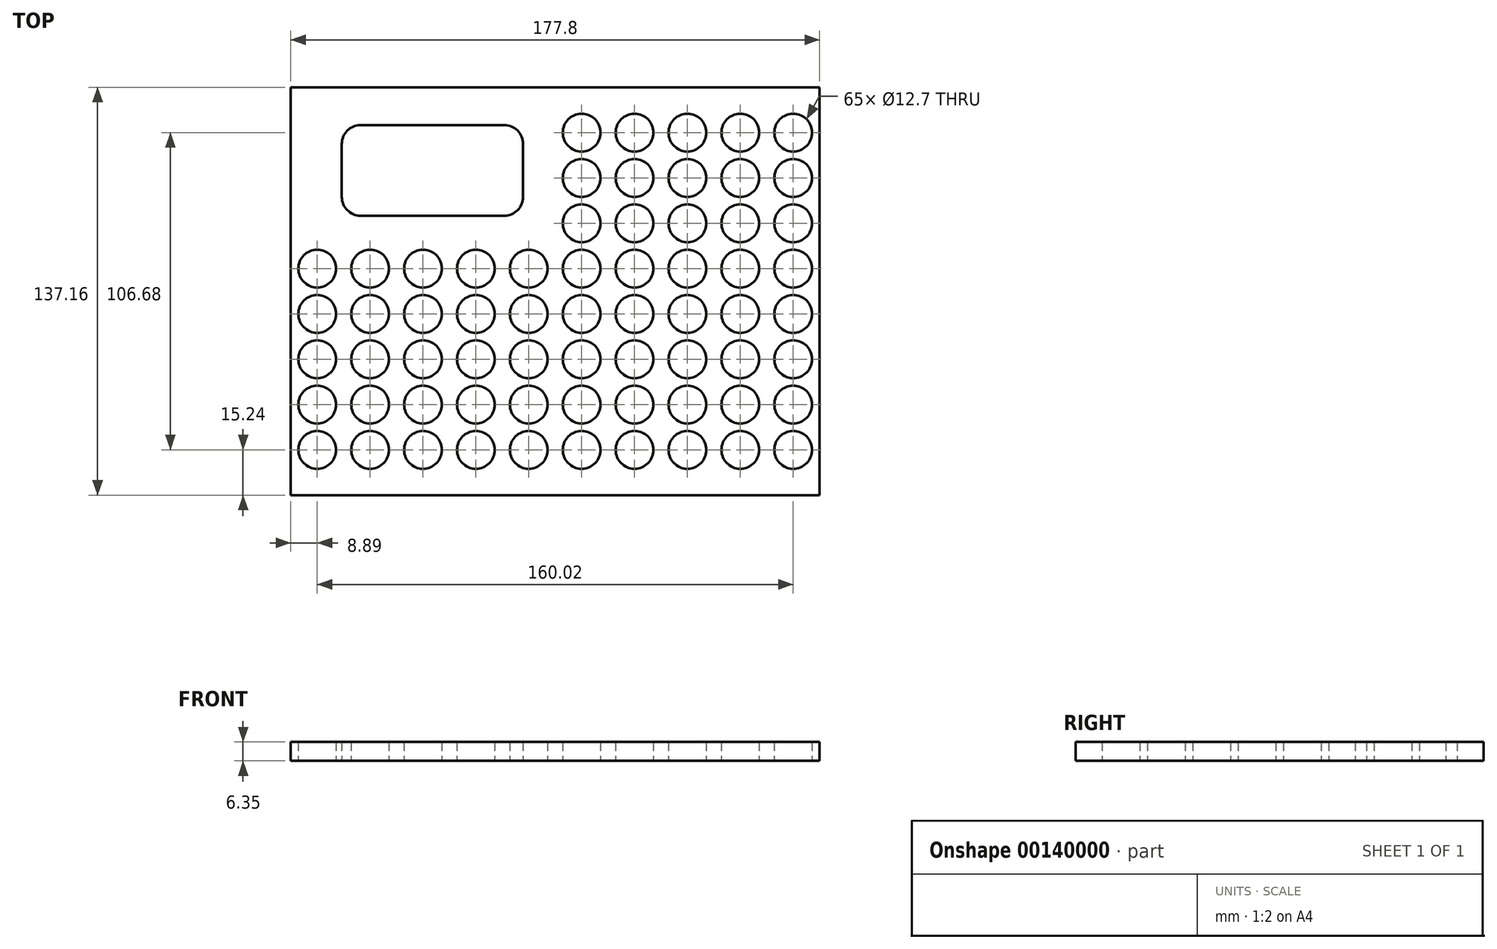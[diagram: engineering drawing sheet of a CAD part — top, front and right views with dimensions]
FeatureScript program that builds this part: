
annotation { "Feature Type Name" : "Feature", "Feature Type Description" : "" }
export const myFeature = defineFeature(function(context is Context, id is Id, definition is map)
    precondition{}
    {
        {
            var Q0;
            Q0=qCreatedBy(makeId("Top.planeOp"),FACE);
            var sketch = newSketch(context, id + "F0", { "sketchPlane" : qUnion([Q0])});
            skCircle(sketch, "E0", {"center": v(0, 0) * mm, "radius": 6.35 * mm});
            skCircle(sketch, "E1.0.1.0", {"center": v(0, 15.24) * mm, "radius": 6.35 * mm});
            skCircle(sketch, "E1.0.2.0", {"center": v(0, 30.48) * mm, "radius": 6.35 * mm});
            skCircle(sketch, "E1.0.3.0", {"center": v(0, 45.72) * mm, "radius": 6.35 * mm});
            skCircle(sketch, "E1.0.4.0", {"center": v(0, 60.96) * mm, "radius": 6.35 * mm});
            skCircle(sketch, "E1.1.0.0", {"center": v(17.78, 0) * mm, "radius": 6.35 * mm});
            skCircle(sketch, "E1.1.1.0", {"center": v(17.78, 15.24) * mm, "radius": 6.35 * mm});
            skCircle(sketch, "E1.1.2.0", {"center": v(17.78, 30.48) * mm, "radius": 6.35 * mm});
            skCircle(sketch, "E1.1.3.0", {"center": v(17.78, 45.72) * mm, "radius": 6.35 * mm});
            skCircle(sketch, "E1.1.4.0", {"center": v(17.78, 60.96) * mm, "radius": 6.35 * mm});
            skCircle(sketch, "E1.2.0.0", {"center": v(35.56, 0) * mm, "radius": 6.35 * mm});
            skCircle(sketch, "E1.2.1.0", {"center": v(35.56, 15.24) * mm, "radius": 6.35 * mm});
            skCircle(sketch, "E1.2.2.0", {"center": v(35.56, 30.48) * mm, "radius": 6.35 * mm});
            skCircle(sketch, "E1.2.3.0", {"center": v(35.56, 45.72) * mm, "radius": 6.35 * mm});
            skCircle(sketch, "E1.2.4.0", {"center": v(35.56, 60.96) * mm, "radius": 6.35 * mm});
            skCircle(sketch, "E1.3.0.0", {"center": v(53.34, 0) * mm, "radius": 6.35 * mm});
            skCircle(sketch, "E1.3.1.0", {"center": v(53.34, 15.24) * mm, "radius": 6.35 * mm});
            skCircle(sketch, "E1.3.2.0", {"center": v(53.34, 30.48) * mm, "radius": 6.35 * mm});
            skCircle(sketch, "E1.3.3.0", {"center": v(53.34, 45.72) * mm, "radius": 6.35 * mm});
            skCircle(sketch, "E1.3.4.0", {"center": v(53.34, 60.96) * mm, "radius": 6.35 * mm});
            skCircle(sketch, "E1.4.0.0", {"center": v(71.12, 0) * mm, "radius": 6.35 * mm});
            skCircle(sketch, "E1.4.1.0", {"center": v(71.12, 15.24) * mm, "radius": 6.35 * mm});
            skCircle(sketch, "E1.4.2.0", {"center": v(71.12, 30.48) * mm, "radius": 6.35 * mm});
            skCircle(sketch, "E1.4.3.0", {"center": v(71.12, 45.72) * mm, "radius": 6.35 * mm});
            skCircle(sketch, "E1.4.4.0", {"center": v(71.12, 60.96) * mm, "radius": 6.35 * mm});
            skCircle(sketch, "E1.5.0.0", {"center": v(88.9, 0) * mm, "radius": 6.35 * mm});
            skCircle(sketch, "E1.5.1.0", {"center": v(88.9, 15.24) * mm, "radius": 6.35 * mm});
            skCircle(sketch, "E1.5.2.0", {"center": v(88.9, 30.48) * mm, "radius": 6.35 * mm});
            skCircle(sketch, "E1.5.3.0", {"center": v(88.9, 45.72) * mm, "radius": 6.35 * mm});
            skCircle(sketch, "E1.5.4.0", {"center": v(88.9, 60.96) * mm, "radius": 6.35 * mm});
            skCircle(sketch, "E1.6.0.0", {"center": v(106.68, 0) * mm, "radius": 6.35 * mm});
            skCircle(sketch, "E1.6.1.0", {"center": v(106.68, 15.24) * mm, "radius": 6.35 * mm});
            skCircle(sketch, "E1.6.2.0", {"center": v(106.68, 30.48) * mm, "radius": 6.35 * mm});
            skCircle(sketch, "E1.6.3.0", {"center": v(106.68, 45.72) * mm, "radius": 6.35 * mm});
            skCircle(sketch, "E1.6.4.0", {"center": v(106.68, 60.96) * mm, "radius": 6.35 * mm});
            skCircle(sketch, "E1.7.0.0", {"center": v(124.46, 0) * mm, "radius": 6.35 * mm});
            skCircle(sketch, "E1.7.1.0", {"center": v(124.46, 15.24) * mm, "radius": 6.35 * mm});
            skCircle(sketch, "E1.7.2.0", {"center": v(124.46, 30.48) * mm, "radius": 6.35 * mm});
            skCircle(sketch, "E1.7.3.0", {"center": v(124.46, 45.72) * mm, "radius": 6.35 * mm});
            skCircle(sketch, "E1.7.4.0", {"center": v(124.46, 60.96) * mm, "radius": 6.35 * mm});
            skLineSegment(sketch, "E1.direction1", {"start": v(0, 0) * mm, "end": v(17.78, 0) * mm, "construction": true});
            skLineSegment(sketch, "E1.direction2", {"start": v(0, 0) * mm, "end": v(0, 15.24) * mm, "construction": true});
            skCircle(sketch, "E2.0.8.0", {"center": v(142.24, 0) * mm, "radius": 6.35 * mm});
            skCircle(sketch, "E2.0.8.1", {"center": v(142.24, 15.24) * mm, "radius": 6.35 * mm});
            skCircle(sketch, "E2.0.8.2", {"center": v(142.24, 30.48) * mm, "radius": 6.35 * mm});
            skCircle(sketch, "E2.0.8.3", {"center": v(142.24, 45.72) * mm, "radius": 6.35 * mm});
            skCircle(sketch, "E2.0.8.4", {"center": v(142.24, 60.96) * mm, "radius": 6.35 * mm});
            skCircle(sketch, "E2.0.9.0", {"center": v(160.02, 0) * mm, "radius": 6.35 * mm});
            skCircle(sketch, "E2.0.9.1", {"center": v(160.02, 15.24) * mm, "radius": 6.35 * mm});
            skCircle(sketch, "E2.0.9.2", {"center": v(160.02, 30.48) * mm, "radius": 6.35 * mm});
            skCircle(sketch, "E2.0.9.3", {"center": v(160.02, 45.72) * mm, "radius": 6.35 * mm});
            skCircle(sketch, "E2.0.9.4", {"center": v(160.02, 60.96) * mm, "radius": 6.35 * mm});
            skLineSegment(sketch, "E3.bottom", {"start": v(-8.9, 121.92) * mm, "end": v(168.9, 121.92) * mm});
            skLineSegment(sketch, "E3.top", {"start": v(-8.89, -15.24) * mm, "end": v(168.9, -15.24) * mm});
            skLineSegment(sketch, "E4", {"start": v(-8.89, 121.92) * mm, "end": v(-8.89, -15.24) * mm});
            skLineSegment(sketch, "E5", {"start": v(168.9, 121.92) * mm, "end": v(168.9, -15.24) * mm});
            skLineSegment(sketch, "E6.bottom", {"start": v(14.6, 109.22) * mm, "end": v(62.87, 109.22) * mm});
            skLineSegment(sketch, "E6.top", {"start": v(14.6, 78.74) * mm, "end": v(62.87, 78.74) * mm});
            skLineSegment(sketch, "E6.left", {"start": v(8.25, 102.87) * mm, "end": v(8.25, 85.09) * mm});
            skLineSegment(sketch, "E6.right", {"start": v(69.22, 102.87) * mm, "end": v(69.22, 85.09) * mm});
            skCircle(sketch, "E7.6.4.0", {"center": v(106.68, 76.2) * mm, "radius": 6.35 * mm});
            skCircle(sketch, "E8.6.4.0", {"center": v(88.9, 76.2) * mm, "radius": 6.35 * mm});
            skCircle(sketch, "E9.6.4.0", {"center": v(124.46, 76.2) * mm, "radius": 6.35 * mm});
            skCircle(sketch, "E10.6.4.0", {"center": v(142.24, 76.2) * mm, "radius": 6.35 * mm});
            skCircle(sketch, "E11.6.4.0", {"center": v(160.02, 76.2) * mm, "radius": 6.35 * mm});
            skCircle(sketch, "E12.6.4.0", {"center": v(106.68, 91.44) * mm, "radius": 6.35 * mm});
            skCircle(sketch, "E13.6.4.0", {"center": v(88.9, 91.44) * mm, "radius": 6.35 * mm});
            skCircle(sketch, "E14.6.4.0", {"center": v(124.46, 91.44) * mm, "radius": 6.35 * mm});
            skCircle(sketch, "E15.6.4.0", {"center": v(142.24, 91.44) * mm, "radius": 6.35 * mm});
            skCircle(sketch, "E16.6.4.0", {"center": v(160.02, 91.44) * mm, "radius": 6.35 * mm});
            skCircle(sketch, "E17.6.4.0", {"center": v(106.68, 106.68) * mm, "radius": 6.35 * mm});
            skCircle(sketch, "E18.6.4.0", {"center": v(88.9, 106.68) * mm, "radius": 6.35 * mm});
            skCircle(sketch, "E19.6.4.0", {"center": v(124.46, 106.68) * mm, "radius": 6.35 * mm});
            skCircle(sketch, "E20.6.4.0", {"center": v(142.24, 106.68) * mm, "radius": 6.35 * mm});
            skCircle(sketch, "E21.6.4.0", {"center": v(160.02, 106.68) * mm, "radius": 6.35 * mm});
            skPoint(sketch, "E22.visualSharp", {"position": v(8.25, 109.22) * mm});
            skArc(sketch, "E22.filletArc", {"start": v(14.6, 109.22) * mm, "mid": v(10.11, 107.36) * mm, "end": v(8.26, 102.87) * mm});
            skPoint(sketch, "E23.visualSharp", {"position": v(69.22, 109.22) * mm});
            skArc(sketch, "E23.filletArc", {"start": v(69.22, 102.87) * mm, "mid": v(67.36, 107.36) * mm, "end": v(62.87, 109.22) * mm});
            skPoint(sketch, "E24.visualSharp", {"position": v(69.22, 78.74) * mm});
            skArc(sketch, "E24.filletArc", {"start": v(62.87, 78.74) * mm, "mid": v(67.36, 80.6) * mm, "end": v(69.22, 85.09) * mm});
            skPoint(sketch, "E25.visualSharp", {"position": v(8.26, 78.74) * mm});
            skArc(sketch, "E25.filletArc", {"start": v(8.26, 85.09) * mm, "mid": v(10.11, 80.6) * mm, "end": v(14.6, 78.74) * mm});
            skSolve(sketch);
        }
        {
            var Q0;
            Q0 = qSketchRegion(id + "F0", true);
            extrude(context, id + "F1", {"entities" : qUnion([Q0]), "depth" : 6.35 * mm});
        }
    });
